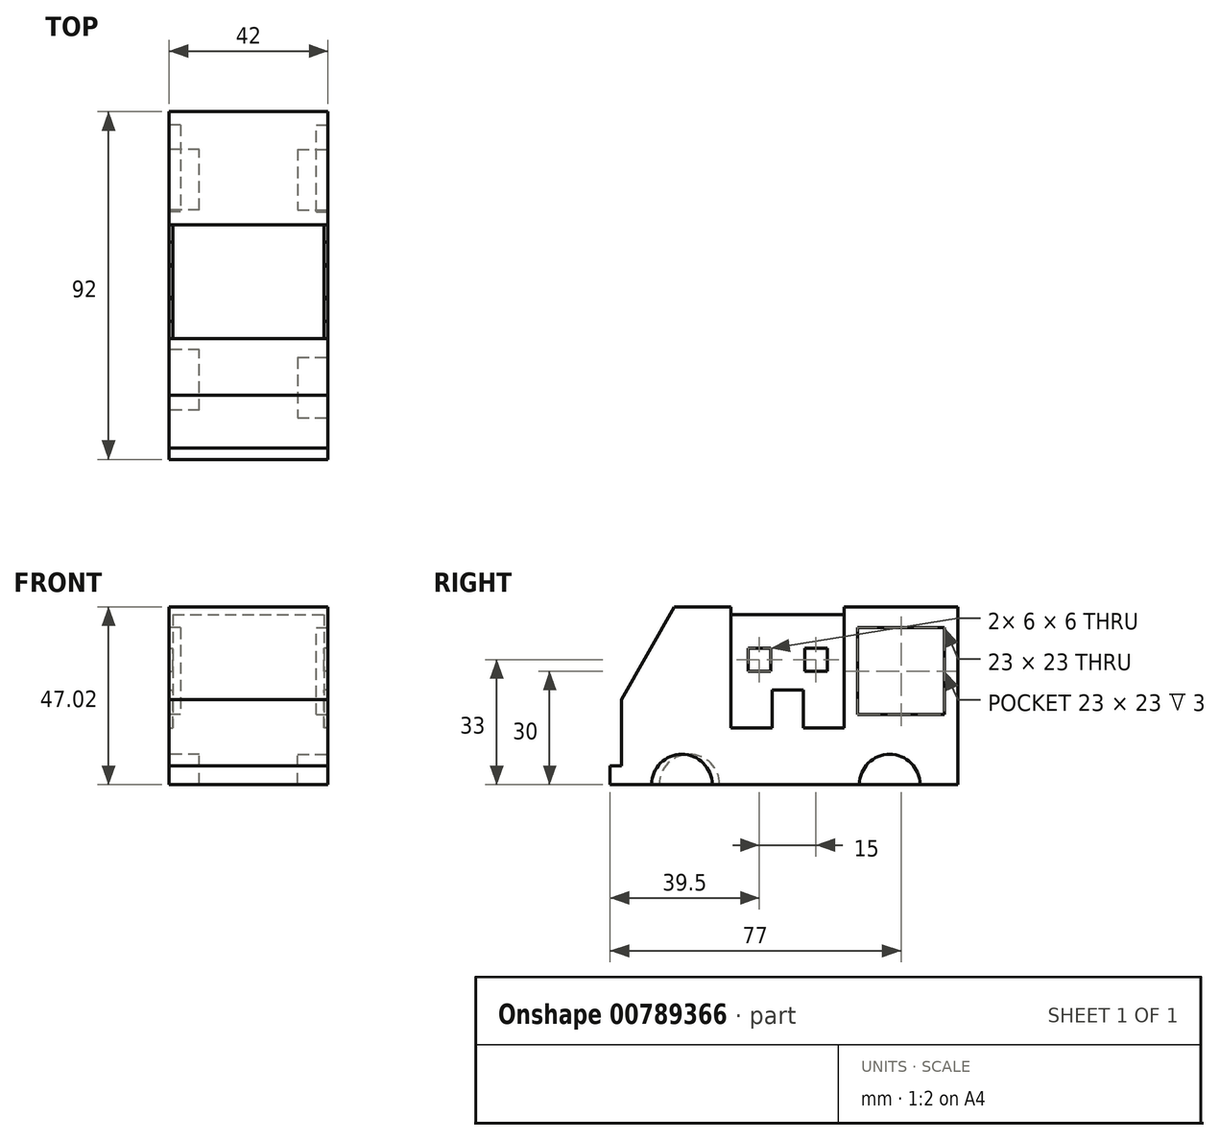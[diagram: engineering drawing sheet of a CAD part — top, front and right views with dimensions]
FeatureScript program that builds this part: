
annotation { "Feature Type Name" : "Feature", "Feature Type Description" : "" }
export const myFeature = defineFeature(function(context is Context, id is Id, definition is map)
    precondition{}
    {
        {
            var Q0;
            Q0=qCreatedBy(makeId("Right.planeOp"),FACE);
            var sketch = newSketch(context, id + "F0", { "sketchPlane" : qUnion([Q0])});
            skLineSegment(sketch, "E0.bottom", {"start": v(15, 22.5) * mm, "end": v(-15, 22.5) * mm});
            skLineSegment(sketch, "E0.top", {"start": v(15, -22.5) * mm, "end": v(-15, -22.5) * mm});
            skLineSegment(sketch, "E0.left", {"start": v(15, 22.5) * mm, "end": v(15, -22.5) * mm});
            skLineSegment(sketch, "E0.right", {"start": v(-15, 22.5) * mm, "end": v(-15, -22.5) * mm});
            skPoint(sketch, "E0.middle", {"position": v(0, 0) * mm});
            skSolve(sketch);
        }
        {
            var Q0;
            Q0 = qSketchRegion(id + "F0", true);
            extrude(context, id + "F1", {"entities" : qUnion([Q0]), "endBound" : BoundingType.SYMMETRIC, "depth" : 40 * mm, "offsetDistance" : 25 * mm});
        }
        {
            var Q0;
            Q0=makeQuery(id+"F1.opExtrude","CAP_FACE",FACE,{"disambiguationData":[OSD([sQuery(id+"F0.wireOp",EDGE,"E0.bottom"),sQuery(id+"F0.wireOp",EDGE,"E0.top"),sQuery(id+"F0.wireOp",EDGE,"E0.left"),sQuery(id+"F0.wireOp",EDGE,"E0.right")])],"isStart":true});
            var sketch = newSketch(context, id + "F2", { "sketchPlane" : qUnion([Q0])});
            skLineSegment(sketch, "E1.bottom", {"start": v(-15, -22.5) * mm, "end": v(15, -22.5) * mm});
            skLineSegment(sketch, "E1.top", {"start": v(-15, -7.5) * mm, "end": v(-4.09, -7.5) * mm});
            skLineSegment(sketch, "E1.left", {"start": v(-15, -22.5) * mm, "end": v(-15, -7.5) * mm});
            skLineSegment(sketch, "E1.right", {"start": v(15, -22.5) * mm, "end": v(15, -7.5) * mm});
            skLineSegment(sketch, "E2.left", {"start": v(4.09, -7.5) * mm, "end": v(4.09, 2.5) * mm});
            skLineSegment(sketch, "E2.right", {"start": v(-4.09, -7.5) * mm, "end": v(-4.09, 2.5) * mm});
            skPoint(sketch, "E2.middle", {"position": v(0, 0) * mm});
            skPoint(sketch, "E3.orphan", {"position": v(-4.09, 7.5) * mm});
            skPoint(sketch, "E4.orphan", {"position": v(4.09, 7.5) * mm});
            skLineSegment(sketch, "E5", {"start": v(-4.09, 2.5) * mm, "end": v(4.09, 2.5) * mm});
            skLineSegment(sketch, "E6", {"start": v(-15, -7.5) * mm, "end": v(-15, -22.5) * mm});
            skLineSegment(sketch, "E7", {"start": v(15, -7.5) * mm, "end": v(15, -22.5) * mm});
            skLineSegment(sketch, "E8", {"start": v(15, -22.5) * mm, "end": v(-15, -22.5) * mm});
            skLineSegment(sketch, "E9.trimOffspring", {"start": v(4.09, -7.5) * mm, "end": v(15, -7.5) * mm});
            skLineSegment(sketch, "E10.bottom", {"start": v(-4.5, 7.5) * mm, "end": v(-10.5, 7.5) * mm});
            skLineSegment(sketch, "E10.top", {"start": v(-4.5, 13.5) * mm, "end": v(-10.5, 13.5) * mm});
            skLineSegment(sketch, "E10.left", {"start": v(-4.5, 7.5) * mm, "end": v(-4.5, 13.5) * mm});
            skLineSegment(sketch, "E10.right", {"start": v(-10.5, 7.5) * mm, "end": v(-10.5, 13.5) * mm});
            skPoint(sketch, "E10.middle", {"position": v(-7.5, 10.5) * mm});
            skLineSegment(sketch, "E11.bottom", {"start": v(4.5, 7.5) * mm, "end": v(10.5, 7.5) * mm});
            skLineSegment(sketch, "E11.top", {"start": v(4.5, 13.5) * mm, "end": v(10.5, 13.5) * mm});
            skLineSegment(sketch, "E11.left", {"start": v(4.5, 7.5) * mm, "end": v(4.5, 13.5) * mm});
            skLineSegment(sketch, "E11.right", {"start": v(10.5, 7.5) * mm, "end": v(10.5, 13.5) * mm});
            skPoint(sketch, "E11.middle", {"position": v(7.5, 10.5) * mm});
            skSolve(sketch);
        }
        {
            var Q0;
            Q0 = qSketchRegion(id + "F2", true);
            extrude(context, id + "F3", {"entities" : qUnion([Q0]), "operationType" : NewBodyOperationType.ADD, "endBound" : BoundingType.SYMMETRIC, "depth" : 2 * mm, "offsetDistance" : 25 * mm});
        }
        {
            var Q0;
            Q0=makeQuery(id+"F1.opExtrude","CAP_FACE",FACE,{"disambiguationData":[OSD([sQuery(id+"F0.wireOp",EDGE,"E0.bottom"),sQuery(id+"F0.wireOp",EDGE,"E0.top"),sQuery(id+"F0.wireOp",EDGE,"E0.left"),sQuery(id+"F0.wireOp",EDGE,"E0.right")])],"isStart":false});
            var sketch = newSketch(context, id + "F4", { "sketchPlane" : qUnion([Q0])});
            skLineSegment(sketch, "E12", {"start": v(-15, -7.5) * mm, "end": v(-4.09, -7.5) * mm});
            skLineSegment(sketch, "E13", {"start": v(-4.09, 2.5) * mm, "end": v(4.09, 2.5) * mm});
            skLineSegment(sketch, "E14", {"start": v(15, -7.5) * mm, "end": v(4.09, -7.5) * mm});
            skLineSegment(sketch, "E15", {"start": v(-4.09, 2.5) * mm, "end": v(-4.09, -7.5) * mm});
            skLineSegment(sketch, "E16", {"start": v(4.09, 2.5) * mm, "end": v(4.09, -7.5) * mm});
            skSolve(sketch);
        }
        {
            var Q0;
            {var subQ1=sQuery(id+"F4.wireOp",EDGE,"E12");Q0=makeQuery(id+"F4.imprint","IMPRINT",FACE,{"disambiguationData":[TD([[makeQuery(id+"F4.imprint","IMPRINT",EDGE,{"derivedFrom":subQ1}),-1.0]])]});}
            extrude(context, id + "F5", {"entities" : qUnion([Q0]), "operationType" : NewBodyOperationType.ADD, "endBound" : BoundingType.SYMMETRIC, "depth" : 2 * mm, "offsetDistance" : 25 * mm});
        }
        {
            var Q0;
            {var subQ0=sQuery(id+"F0.wireOp",EDGE,"E0.left");Q0=makeQuery(id+"F5.boolean.opBoolean","MERGE",FACE,{"derivedFrom":[makeQuery(id+"F3.boolean.opBoolean","MERGE",FACE,{"derivedFrom":[makeQuery(id+"F1.opExtrude","SWEPT_FACE",FACE,{"disambiguationData":[OSD([subQ0])]}),makeQuery(id+"F3.opExtrude","SWEPT_FACE",FACE,{"disambiguationData":[OSD([sQuery(id+"F2.wireOp",EDGE,"E6")])]})]}),makeQuery(id+"F5.opExtrude","SWEPT_FACE",FACE,{"disambiguationData":[OSD([subQ0])]})]});}
            var sketch = newSketch(context, id + "F6", { "sketchPlane" : qUnion([Q0])});
            skLineSegment(sketch, "E17", {"start": v(21, -22.5) * mm, "end": v(21, 22.5) * mm});
            skLineSegment(sketch, "E18", {"start": v(21, 22.5) * mm, "end": v(20, 22.5) * mm});
            skLineSegment(sketch, "E19", {"start": v(20, 22.5) * mm, "end": v(-21, 22.5) * mm});
            skLineSegment(sketch, "E20", {"start": v(-21, 22.5) * mm, "end": v(-21, -22.5) * mm});
            skSolve(sketch);
        }
        {
            var Q0;
            Q0 = qSketchRegion(id + "F6", true);
            var Q1;
            {var subQ3=sQuery(id+"F6.wireOp",EDGE,"E18");Q1=makeQuery(id+"F6.imprint","IMPRINT",FACE,{"disambiguationData":[TD([[makeQuery(id+"F6.imprint","IMPRINT",EDGE,{"derivedFrom":subQ3}),1.0]])]});}
            var Q2;
            {var subQ0=sQuery(id+"F0.wireOp",EDGE,"E0.left");var subQ1=makeQuery(id+"F1.opExtrude","CAP_EDGE",EDGE,{"disambiguationData":[OSD([subQ0])],"isStart":true});Q2=makeQuery(id+"F6.imprint","IMPRINT",FACE,{"disambiguationData":[TD([[makeQuery(id+"F6.imprint","IMPRINT",EDGE,{"derivedFrom":subQ1}),-1.0]])]});}
            var Q3;
            {var subQ1=sQuery(id+"F0.wireOp",EDGE,"E0.left");var subQ2=makeQuery(id+"F1.opExtrude","CAP_EDGE",EDGE,{"disambiguationData":[OSD([subQ1])],"isStart":false});Q3=makeQuery(id+"F6.imprint","IMPRINT",FACE,{"disambiguationData":[TD([[makeQuery(id+"F6.imprint","IMPRINT",EDGE,{"derivedFrom":subQ2}),-1.0]])]});}
            extrude(context, id + "F7", {"entities" : qUnion([Q0, Q1, Q2, Q3]), "operationType" : NewBodyOperationType.ADD, "depth" : 30 * mm, "offsetDistance" : 25 * mm});
        }
        {
            var Q0;
            Q0=makeQuery(id+"F7.boolean.opBoolean","MERGE",FACE,{"derivedFrom":[makeQuery(id+"F3.opExtrude","CAP_FACE",FACE,{"disambiguationData":[OSD([sQuery(id+"F2.wireOp",EDGE,"E1.top"),sQuery(id+"F2.wireOp",EDGE,"E2.left"),sQuery(id+"F2.wireOp",EDGE,"E2.right"),sQuery(id+"F2.wireOp",EDGE,"E5"),sQuery(id+"F2.wireOp",EDGE,"E6"),sQuery(id+"F2.wireOp",EDGE,"E7"),sQuery(id+"F2.wireOp",EDGE,"E8"),sQuery(id+"F2.wireOp",EDGE,"E9.trimOffspring")])],"isStart":false}),makeQuery(id+"F7.opExtrude","SWEPT_FACE",FACE,{"disambiguationData":[OSD([sQuery(id+"F6.wireOp",EDGE,"E17")])]})]});
            var sketch = newSketch(context, id + "F8", { "sketchPlane" : qUnion([Q0])});
            skPoint(sketch, "E21.0", {"position": v(-45, 22.5) * mm});
            skPoint(sketch, "E22.0", {"position": v(-15, -7.5) * mm});
            skLineSegment(sketch, "E23.0", {"start": v(-15, -7.5) * mm, "end": v(-15, 22.5) * mm});
            skLineSegment(sketch, "E24.bottom", {"start": v(-41.5, 19) * mm, "end": v(-18.5, 19) * mm});
            skLineSegment(sketch, "E24.top", {"start": v(-41.5, -4) * mm, "end": v(-18.5, -4) * mm});
            skLineSegment(sketch, "E24.left", {"start": v(-41.5, 19) * mm, "end": v(-41.5, -4) * mm});
            skLineSegment(sketch, "E24.right", {"start": v(-18.5, 19) * mm, "end": v(-18.5, -4) * mm});
            skPoint(sketch, "E24.middle", {"position": v(-30, 7.5) * mm});
            skPoint(sketch, "E25.trimOffspring.end.orphan", {"position": v(-45, -7.5) * mm});
            skLineSegment(sketch, "E26", {"start": v(-18.5, 19) * mm, "end": v(-41.5, 19) * mm});
            skSolve(sketch);
        }
        {
            var Q0;
            Q0=makeQuery(id+"F8.imprint","IMPRINT",FACE,{"disambiguationData":[TD([[makeQuery(id+"F8.imprint","IMPRINT",EDGE,{"derivedFrom":sQuery(id+"F8.wireOp",EDGE,"E24.left")}),1.0]])]});
            extrude(context, id + "F9", {"entities" : qUnion([Q0]), "operationType" : NewBodyOperationType.REMOVE, "oppositeDirection" : true, "depth" : 3 * mm, "offsetDistance" : 25 * mm});
        }
        {
            var Q0;
            Q0=makeQuery(id+"F7.boolean.opBoolean","MERGE",FACE,{"derivedFrom":[makeQuery(id+"F5.opExtrude","CAP_FACE",FACE,{"disambiguationData":[OSD([sQuery(id+"F0.wireOp",EDGE,"E0.top"),sQuery(id+"F0.wireOp",EDGE,"E0.left"),sQuery(id+"F0.wireOp",EDGE,"E0.right"),sQuery(id+"F4.wireOp",EDGE,"E12"),sQuery(id+"F4.wireOp",EDGE,"E13"),sQuery(id+"F4.wireOp",EDGE,"E14"),sQuery(id+"F4.wireOp",EDGE,"E15"),sQuery(id+"F4.wireOp",EDGE,"E16")])],"isStart":false}),makeQuery(id+"F7.opExtrude","SWEPT_FACE",FACE,{"disambiguationData":[OSD([sQuery(id+"F6.wireOp",EDGE,"E20")])]})]});
            var sketch = newSketch(context, id + "F10", { "sketchPlane" : qUnion([Q0])});
            skLineSegment(sketch, "E27", {"start": v(18.5, 19) * mm, "end": v(41.5, 19) * mm});
            skLineSegment(sketch, "E28", {"start": v(41.5, 19) * mm, "end": v(41.5, -4) * mm});
            skLineSegment(sketch, "E29", {"start": v(41.5, -4) * mm, "end": v(18.5, -4) * mm});
            skLineSegment(sketch, "E30", {"start": v(18.5, -4) * mm, "end": v(18.5, 19) * mm});
            skSolve(sketch);
        }
        {
            var Q0;
            Q0=makeQuery(id+"F10.imprint","IMPRINT",FACE,{"disambiguationData":[TD([[makeQuery(id+"F10.imprint","IMPRINT",EDGE,{"derivedFrom":sQuery(id+"F10.wireOp",EDGE,"E27")}),-1.0]])]});
            extrude(context, id + "F11", {"entities" : qUnion([Q0]), "operationType" : NewBodyOperationType.REMOVE, "oppositeDirection" : true, "depth" : 3 * mm, "offsetDistance" : 25 * mm});
        }
        {
            var Q0;
            Q0=makeQuery(id+"F7.boolean.opBoolean","MERGE",FACE,{"derivedFrom":[makeQuery(id+"F1.opExtrude","SWEPT_FACE",FACE,{"disambiguationData":[OSD([sQuery(id+"F0.wireOp",EDGE,"E0.bottom")])]}),makeQuery(id+"F7.opExtrude","SWEPT_FACE",FACE,{"disambiguationData":[OSD([sQuery(id+"F6.wireOp",EDGE,"E18"),sQuery(id+"F6.wireOp",EDGE,"E19")])]})]});
            var sketch = newSketch(context, id + "F12", { "sketchPlane" : qUnion([Q0])});
            skLineSegment(sketch, "E31.bottom", {"start": v(-21, 45) * mm, "end": v(21, 45) * mm});
            skLineSegment(sketch, "E31.top", {"start": v(-21, 15) * mm, "end": v(21, 15) * mm});
            skLineSegment(sketch, "E31.left", {"start": v(-21, 45) * mm, "end": v(-21, 15) * mm});
            skLineSegment(sketch, "E31.right", {"start": v(21, 45) * mm, "end": v(21, 15) * mm});
            skSolve(sketch);
        }
        {
            var Q0;
            Q0 = qSketchRegion(id + "F12", true);
            extrude(context, id + "F13", {"entities" : qUnion([Q0]), "operationType" : NewBodyOperationType.ADD, "depth" : 2 * mm, "offsetDistance" : 25 * mm});
        }
        {
            var Q0;
            Q0=makeQuery(id+"F13.boolean.opBoolean","MERGE",FACE,{"derivedFrom":[makeQuery(id+"F7.boolean.opBoolean","MERGE",FACE,{"derivedFrom":[makeQuery(id+"F3.opExtrude","CAP_FACE",FACE,{"disambiguationData":[OSD([sQuery(id+"F2.wireOp",EDGE,"E1.top"),sQuery(id+"F2.wireOp",EDGE,"E2.left"),sQuery(id+"F2.wireOp",EDGE,"E2.right"),sQuery(id+"F2.wireOp",EDGE,"E5"),sQuery(id+"F2.wireOp",EDGE,"E6"),sQuery(id+"F2.wireOp",EDGE,"E7"),sQuery(id+"F2.wireOp",EDGE,"E8"),sQuery(id+"F2.wireOp",EDGE,"E9.trimOffspring")])],"isStart":false}),makeQuery(id+"F7.opExtrude","SWEPT_FACE",FACE,{"disambiguationData":[OSD([sQuery(id+"F6.wireOp",EDGE,"E17")])]})]}),makeQuery(id+"F13.opExtrude","SWEPT_FACE",FACE,{"disambiguationData":[OSD([sQuery(id+"F12.wireOp",EDGE,"E31.left")])]})]});
            var sketch = newSketch(context, id + "F14", { "sketchPlane" : qUnion([Q0])});
            skCircle(sketch, "E32", {"center": v(-27, -22.5) * mm, "radius": 8 * mm});
            skSolve(sketch);
        }
        {
            var Q0;
            Q0 = qSketchRegion(id + "F14", true);
            extrude(context, id + "F15", {"entities" : qUnion([Q0]), "operationType" : NewBodyOperationType.REMOVE, "oppositeDirection" : true, "depth" : 8 * mm, "offsetDistance" : 25 * mm});
        }
        {
            var Q0;
            {var subQ0=sQuery(id+"F0.wireOp",EDGE,"E0.right");Q0=makeQuery(id+"F5.boolean.opBoolean","MERGE",FACE,{"derivedFrom":[makeQuery(id+"F3.boolean.opBoolean","MERGE",FACE,{"derivedFrom":[makeQuery(id+"F1.opExtrude","SWEPT_FACE",FACE,{"disambiguationData":[OSD([subQ0])]}),makeQuery(id+"F3.opExtrude","SWEPT_FACE",FACE,{"disambiguationData":[OSD([sQuery(id+"F2.wireOp",EDGE,"E7")])]})]}),makeQuery(id+"F5.opExtrude","SWEPT_FACE",FACE,{"disambiguationData":[OSD([subQ0])]})]});}
            var sketch = newSketch(context, id + "F16", { "sketchPlane" : qUnion([Q0])});
            skLineSegment(sketch, "E33.bottom", {"start": v(-21, -22.5) * mm, "end": v(-21, -22.5) * mm});
            skLineSegment(sketch, "E33.top", {"start": v(-21, 24.52) * mm, "end": v(-21, 24.52) * mm});
            skLineSegment(sketch, "E33.left", {"start": v(-21, -22.5) * mm, "end": v(-21, 24.52) * mm});
            skLineSegment(sketch, "E33.right", {"start": v(-21, -22.5) * mm, "end": v(-21, 24.52) * mm});
            skLineSegment(sketch, "E34", {"start": v(-21, -22.5) * mm, "end": v(21, -22.5) * mm});
            skLineSegment(sketch, "E35", {"start": v(21, -22.5) * mm, "end": v(21, 24.5) * mm});
            skLineSegment(sketch, "E36", {"start": v(21, 24.5) * mm, "end": v(-21, 24.52) * mm});
            skSolve(sketch);
        }
        {
            var Q0;
            Q0 = qSketchRegion(id + "F16", true);
            extrude(context, id + "F17", {"entities" : qUnion([Q0]), "operationType" : NewBodyOperationType.ADD, "depth" : 15 * mm, "offsetDistance" : 25 * mm});
        }
        {
            var Q0;
            Q0=makeQuery(id+"F17.opExtrude","CAP_FACE",FACE,{"disambiguationData":[OSD([sQuery(id+"F16.wireOp",EDGE,"E33.right"),sQuery(id+"F16.wireOp",EDGE,"E34"),sQuery(id+"F16.wireOp",EDGE,"E35"),sQuery(id+"F16.wireOp",EDGE,"E36")])],"isStart":false});
            var sketch = newSketch(context, id + "F18", { "sketchPlane" : qUnion([Q0])});
            skLineSegment(sketch, "E37.bottom", {"start": v(21, -22.5) * mm, "end": v(-21, -22.5) * mm});
            skLineSegment(sketch, "E37.top", {"start": v(21, 0) * mm, "end": v(-21, 0) * mm});
            skLineSegment(sketch, "E37.left", {"start": v(21, -22.5) * mm, "end": v(21, 0) * mm});
            skLineSegment(sketch, "E37.right", {"start": v(-21, -22.5) * mm, "end": v(-21, 0) * mm});
            skSolve(sketch);
        }
        {
            var Q0;
            Q0 = qSketchRegion(id + "F18", true);
            extrude(context, id + "F19", {"entities" : qUnion([Q0]), "operationType" : NewBodyOperationType.ADD, "depth" : 14 * mm, "offsetDistance" : 25 * mm});
        }
        {
            var Q0;
            Q0=makeQuery(id+"F19.boolean.opBoolean","MERGE",FACE,{"derivedFrom":[makeQuery(id+"F17.boolean.opBoolean","MERGE",FACE,{"derivedFrom":[makeQuery(id+"F13.boolean.opBoolean","MERGE",FACE,{"derivedFrom":[makeQuery(id+"F7.boolean.opBoolean","MERGE",FACE,{"derivedFrom":[makeQuery(id+"F3.opExtrude","CAP_FACE",FACE,{"disambiguationData":[OSD([sQuery(id+"F2.wireOp",EDGE,"E1.top"),sQuery(id+"F2.wireOp",EDGE,"E2.left"),sQuery(id+"F2.wireOp",EDGE,"E2.right"),sQuery(id+"F2.wireOp",EDGE,"E5"),sQuery(id+"F2.wireOp",EDGE,"E6"),sQuery(id+"F2.wireOp",EDGE,"E7"),sQuery(id+"F2.wireOp",EDGE,"E8"),sQuery(id+"F2.wireOp",EDGE,"E9.trimOffspring")])],"isStart":false}),makeQuery(id+"F7.opExtrude","SWEPT_FACE",FACE,{"disambiguationData":[OSD([sQuery(id+"F6.wireOp",EDGE,"E17")])]})]}),makeQuery(id+"F13.opExtrude","SWEPT_FACE",FACE,{"disambiguationData":[OSD([sQuery(id+"F12.wireOp",EDGE,"E31.left")])]})]}),makeQuery(id+"F17.opExtrude","SWEPT_FACE",FACE,{"disambiguationData":[OSD([sQuery(id+"F16.wireOp",EDGE,"E33.right")])]})]}),makeQuery(id+"F19.opExtrude","SWEPT_FACE",FACE,{"disambiguationData":[OSD([sQuery(id+"F18.wireOp",EDGE,"E37.right")])]})]});
            var sketch = newSketch(context, id + "F20", { "sketchPlane" : qUnion([Q0])});
            skLineSegment(sketch, "E38", {"start": v(30, 24.52) * mm, "end": v(44, 0) * mm});
            skSolve(sketch);
        }
        {
            var Q0;
            Q0=makeQuery(id+"F19.boolean.opBoolean","MERGE",FACE,{"derivedFrom":[makeQuery(id+"F17.boolean.opBoolean","MERGE",FACE,{"derivedFrom":[makeQuery(id+"F13.boolean.opBoolean","MERGE",FACE,{"derivedFrom":[makeQuery(id+"F7.boolean.opBoolean","MERGE",FACE,{"derivedFrom":[makeQuery(id+"F5.opExtrude","CAP_FACE",FACE,{"disambiguationData":[OSD([sQuery(id+"F0.wireOp",EDGE,"E0.top"),sQuery(id+"F0.wireOp",EDGE,"E0.left"),sQuery(id+"F0.wireOp",EDGE,"E0.right"),sQuery(id+"F4.wireOp",EDGE,"E12"),sQuery(id+"F4.wireOp",EDGE,"E13"),sQuery(id+"F4.wireOp",EDGE,"E14"),sQuery(id+"F4.wireOp",EDGE,"E15"),sQuery(id+"F4.wireOp",EDGE,"E16")])],"isStart":false}),makeQuery(id+"F7.opExtrude","SWEPT_FACE",FACE,{"disambiguationData":[OSD([sQuery(id+"F6.wireOp",EDGE,"E20")])]})]}),makeQuery(id+"F13.opExtrude","SWEPT_FACE",FACE,{"disambiguationData":[OSD([sQuery(id+"F12.wireOp",EDGE,"E31.right")])]})]}),makeQuery(id+"F17.opExtrude","SWEPT_FACE",FACE,{"disambiguationData":[OSD([sQuery(id+"F16.wireOp",EDGE,"E35")])]})]}),makeQuery(id+"F19.opExtrude","SWEPT_FACE",FACE,{"disambiguationData":[OSD([sQuery(id+"F18.wireOp",EDGE,"E37.left")])]})]});
            var sketch = newSketch(context, id + "F21", { "sketchPlane" : qUnion([Q0])});
            skCircle(sketch, "E39", {"center": v(27, -22.5) * mm, "radius": 8 * mm});
            skSolve(sketch);
        }
        {
            var Q0;
            Q0 = qSketchRegion(id + "F21", true);
            extrude(context, id + "F22", {"entities" : qUnion([Q0]), "operationType" : NewBodyOperationType.REMOVE, "oppositeDirection" : true, "depth" : 8 * mm, "offsetDistance" : 25 * mm});
        }
        {
            var Q0;
            Q0=makeQuery(id+"F20.imprint","IMPRINT",FACE,{"disambiguationData":[TD([[makeQuery(id+"F20.imprint","IMPRINT",EDGE,{"derivedFrom":sQuery(id+"F20.wireOp",EDGE,"E38")}),-1.0]])]});
            extrude(context, id + "F23", {"entities" : qUnion([Q0]), "operationType" : NewBodyOperationType.ADD, "oppositeDirection" : true, "depth" : 42 * mm, "offsetDistance" : 25 * mm});
        }
        {
            var Q0;
            Q0 = qSketchRegion(id + "F2", true);
            extrude(context, id + "F24", {"entities" : qUnion([Q0]), "operationType" : NewBodyOperationType.ADD, "depth" : 1 * mm, "offsetDistance" : 25 * mm});
        }
        {
            var Q0;
            {var subQ0=sQuery(id+"F18.wireOp",EDGE,"E37.right");var subQ1=sQuery(id+"F16.wireOp",EDGE,"E33.right");Q0=makeQuery(id+"F23.boolean.opBoolean","MERGE",FACE,{"derivedFrom":[makeQuery(id+"F19.boolean.opBoolean","MERGE",FACE,{"derivedFrom":[makeQuery(id+"F17.boolean.opBoolean","MERGE",FACE,{"derivedFrom":[makeQuery(id+"F13.boolean.opBoolean","MERGE",FACE,{"derivedFrom":[makeQuery(id+"F7.boolean.opBoolean","MERGE",FACE,{"derivedFrom":[makeQuery(id+"F3.opExtrude","CAP_FACE",FACE,{"disambiguationData":[OSD([sQuery(id+"F2.wireOp",EDGE,"E1.top"),sQuery(id+"F2.wireOp",EDGE,"E2.left"),sQuery(id+"F2.wireOp",EDGE,"E2.right"),sQuery(id+"F2.wireOp",EDGE,"E5"),sQuery(id+"F2.wireOp",EDGE,"E6"),sQuery(id+"F2.wireOp",EDGE,"E7"),sQuery(id+"F2.wireOp",EDGE,"E8"),sQuery(id+"F2.wireOp",EDGE,"E9.trimOffspring")])],"isStart":false}),makeQuery(id+"F7.opExtrude","SWEPT_FACE",FACE,{"disambiguationData":[OSD([sQuery(id+"F6.wireOp",EDGE,"E17")])]})]}),makeQuery(id+"F13.opExtrude","SWEPT_FACE",FACE,{"disambiguationData":[OSD([sQuery(id+"F12.wireOp",EDGE,"E31.left")])]})]}),makeQuery(id+"F17.opExtrude","SWEPT_FACE",FACE,{"disambiguationData":[OSD([subQ1])]})]}),makeQuery(id+"F19.opExtrude","SWEPT_FACE",FACE,{"disambiguationData":[OSD([subQ0])]})]}),makeQuery(id+"F23.opExtrude","CAP_FACE",FACE,{"disambiguationData":[OSD([subQ1,sQuery(id+"F18.wireOp",EDGE,"E37.top"),subQ0,sQuery(id+"F20.wireOp",EDGE,"E38")])],"isStart":true})]});}
            var sketch = newSketch(context, id + "F25", { "sketchPlane" : qUnion([Q0])});
            skCircle(sketch, "E40", {"center": v(26, -22.5) * mm, "radius": 8 * mm});
            skSolve(sketch);
        }
        {
            var Q0;
            Q0 = qSketchRegion(id + "F25", true);
            extrude(context, id + "F26", {"entities" : qUnion([Q0]), "operationType" : NewBodyOperationType.REMOVE, "oppositeDirection" : true, "depth" : 8 * mm, "offsetDistance" : 25 * mm});
        }
        {
            var Q0;
            Q0=makeQuery(id+"F23.boolean.opBoolean","MERGE",FACE,{"derivedFrom":[makeQuery(id+"F19.boolean.opBoolean","MERGE",FACE,{"derivedFrom":[makeQuery(id+"F17.boolean.opBoolean","MERGE",FACE,{"derivedFrom":[makeQuery(id+"F13.boolean.opBoolean","MERGE",FACE,{"derivedFrom":[makeQuery(id+"F7.boolean.opBoolean","MERGE",FACE,{"derivedFrom":[makeQuery(id+"F5.opExtrude","CAP_FACE",FACE,{"disambiguationData":[OSD([sQuery(id+"F0.wireOp",EDGE,"E0.top"),sQuery(id+"F0.wireOp",EDGE,"E0.left"),sQuery(id+"F0.wireOp",EDGE,"E0.right"),sQuery(id+"F4.wireOp",EDGE,"E12"),sQuery(id+"F4.wireOp",EDGE,"E13"),sQuery(id+"F4.wireOp",EDGE,"E14"),sQuery(id+"F4.wireOp",EDGE,"E15"),sQuery(id+"F4.wireOp",EDGE,"E16")])],"isStart":false}),makeQuery(id+"F7.opExtrude","SWEPT_FACE",FACE,{"disambiguationData":[OSD([sQuery(id+"F6.wireOp",EDGE,"E20")])]})]}),makeQuery(id+"F13.opExtrude","SWEPT_FACE",FACE,{"disambiguationData":[OSD([sQuery(id+"F12.wireOp",EDGE,"E31.right")])]})]}),makeQuery(id+"F17.opExtrude","SWEPT_FACE",FACE,{"disambiguationData":[OSD([sQuery(id+"F16.wireOp",EDGE,"E35")])]})]}),makeQuery(id+"F19.opExtrude","SWEPT_FACE",FACE,{"disambiguationData":[OSD([sQuery(id+"F18.wireOp",EDGE,"E37.left")])]})]}),makeQuery(id+"F23.opExtrude","CAP_FACE",FACE,{"disambiguationData":[OSD([sQuery(id+"F16.wireOp",EDGE,"E33.right"),sQuery(id+"F18.wireOp",EDGE,"E37.top"),sQuery(id+"F18.wireOp",EDGE,"E37.right"),sQuery(id+"F20.wireOp",EDGE,"E38")])],"isStart":false})]});
            var sketch = newSketch(context, id + "F27", { "sketchPlane" : qUnion([Q0])});
            skCircle(sketch, "E41", {"center": v(-28, -22.5) * mm, "radius": 8 * mm});
            skSolve(sketch);
        }
        {
            var Q0;
            Q0 = qSketchRegion(id + "F27", true);
            extrude(context, id + "F28", {"entities" : qUnion([Q0]), "operationType" : NewBodyOperationType.REMOVE, "oppositeDirection" : true, "depth" : 8 * mm, "offsetDistance" : 25 * mm});
        }
        {
            var Q0;
            Q0=makeQuery(id+"F1.opExtrude","CAP_FACE",FACE,{"disambiguationData":[OSD([sQuery(id+"F0.wireOp",EDGE,"E0.bottom"),sQuery(id+"F0.wireOp",EDGE,"E0.top"),sQuery(id+"F0.wireOp",EDGE,"E0.left"),sQuery(id+"F0.wireOp",EDGE,"E0.right")])],"isStart":false});
            var sketch = newSketch(context, id + "F29", { "sketchPlane" : qUnion([Q0])});
            skLineSegment(sketch, "E42.bottom", {"start": v(-10.5, 13.5) * mm, "end": v(-4.5, 13.5) * mm});
            skLineSegment(sketch, "E42.top", {"start": v(-10.5, 7.5) * mm, "end": v(-4.5, 7.5) * mm});
            skLineSegment(sketch, "E42.left", {"start": v(-10.5, 13.5) * mm, "end": v(-10.5, 7.5) * mm});
            skLineSegment(sketch, "E42.right", {"start": v(-4.5, 13.5) * mm, "end": v(-4.5, 7.5) * mm});
            skPoint(sketch, "E42.middle", {"position": v(-7.5, 10.5) * mm});
            skLineSegment(sketch, "E43.bottom", {"start": v(4.5, 13.5) * mm, "end": v(10.5, 13.5) * mm});
            skLineSegment(sketch, "E43.top", {"start": v(4.5, 7.5) * mm, "end": v(10.5, 7.5) * mm});
            skLineSegment(sketch, "E43.left", {"start": v(4.5, 13.5) * mm, "end": v(4.5, 7.5) * mm});
            skLineSegment(sketch, "E43.right", {"start": v(10.5, 13.5) * mm, "end": v(10.5, 7.5) * mm});
            skPoint(sketch, "E43.middle", {"position": v(7.5, 10.5) * mm});
            skSolve(sketch);
        }
        {
            var Q0;
            Q0=makeQuery(id+"F29.imprint","IMPRINT",FACE,{"disambiguationData":[TD([[makeQuery(id+"F29.imprint","IMPRINT",EDGE,{"derivedFrom":sQuery(id+"F29.wireOp",EDGE,"E42.bottom")}),-1.0]])]});
            var Q1;
            Q1=makeQuery(id+"F29.imprint","IMPRINT",FACE,{"disambiguationData":[TD([[makeQuery(id+"F29.imprint","IMPRINT",EDGE,{"derivedFrom":sQuery(id+"F29.wireOp",EDGE,"E43.bottom")}),-1.0]])]});
            extrude(context, id + "F30", {"entities" : qUnion([Q0, Q1]), "operationType" : NewBodyOperationType.ADD, "endBound" : BoundingType.SYMMETRIC, "depth" : 2 * mm, "offsetDistance" : 25 * mm});
        }
        {
            var Q0;
            Q0=makeQuery(id+"F19.opExtrude","CAP_FACE",FACE,{"disambiguationData":[OSD([sQuery(id+"F18.wireOp",EDGE,"E37.bottom"),sQuery(id+"F18.wireOp",EDGE,"E37.top"),sQuery(id+"F18.wireOp",EDGE,"E37.left"),sQuery(id+"F18.wireOp",EDGE,"E37.right")])],"isStart":false});
            var sketch = newSketch(context, id + "F31", { "sketchPlane" : qUnion([Q0])});
            skLineSegment(sketch, "E44.bottom", {"start": v(-21, -22.5) * mm, "end": v(21, -22.5) * mm});
            skLineSegment(sketch, "E44.top", {"start": v(-21, -17.5) * mm, "end": v(21, -17.5) * mm});
            skLineSegment(sketch, "E44.left", {"start": v(-21, -22.5) * mm, "end": v(-21, -17.5) * mm});
            skLineSegment(sketch, "E44.right", {"start": v(21, -22.5) * mm, "end": v(21, -17.5) * mm});
            skSolve(sketch);
        }
        {
            var Q0;
            Q0 = qSketchRegion(id + "F31", true);
            extrude(context, id + "F32", {"entities" : qUnion([Q0]), "operationType" : NewBodyOperationType.ADD, "depth" : 3 * mm, "offsetDistance" : 25 * mm});
        }
    });
